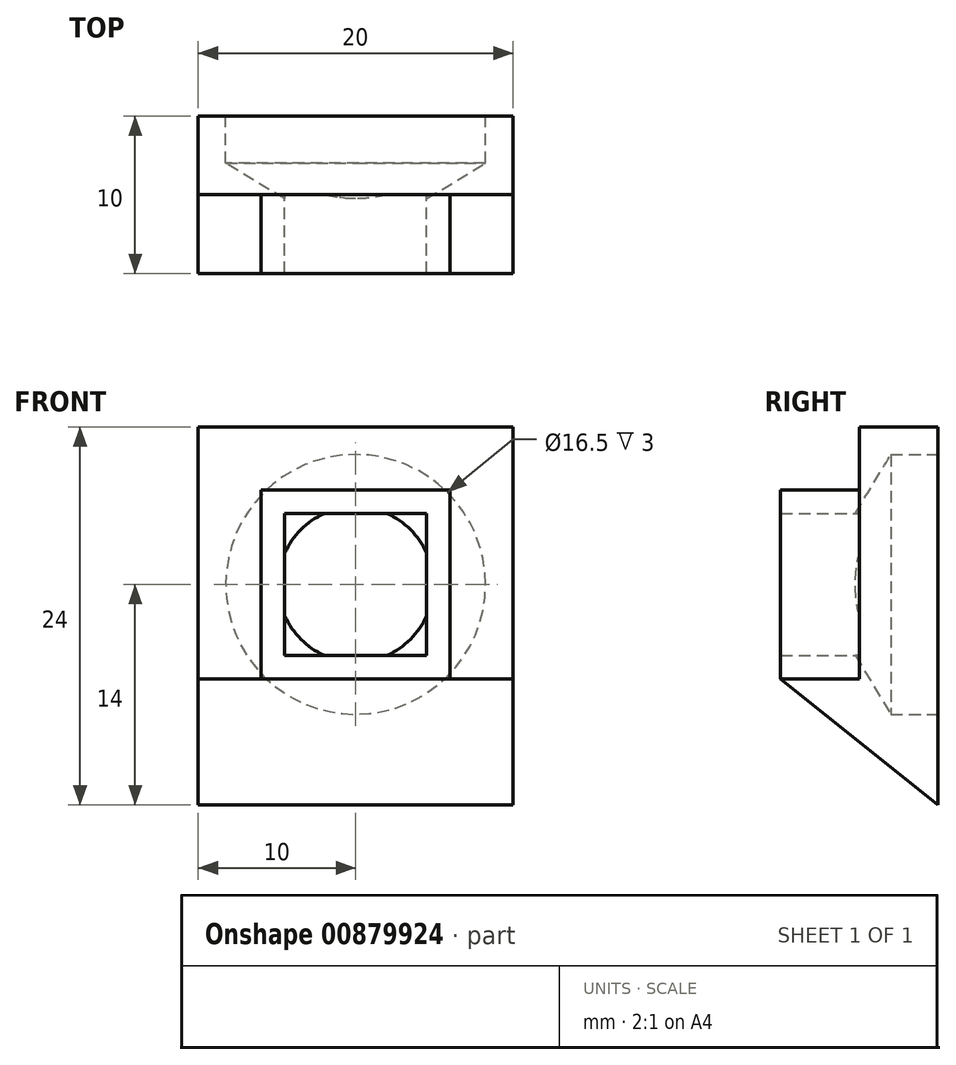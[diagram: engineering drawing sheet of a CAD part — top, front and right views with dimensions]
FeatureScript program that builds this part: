
annotation { "Feature Type Name" : "Feature", "Feature Type Description" : "" }
export const myFeature = defineFeature(function(context is Context, id is Id, definition is map)
    precondition{}
    {
        {
            var Q0;
            Q0=qCreatedBy(makeId("Front.planeOp"),FACE);
            var sketch = newSketch(context, id + "F0", { "sketchPlane" : qUnion([Q0])});
            skLineSegment(sketch, "E0.bottom", {"start": v(10, 10) * mm, "end": v(-10, 10) * mm});
            skLineSegment(sketch, "E0.top", {"start": v(10, -10) * mm, "end": v(-10, -10) * mm});
            skLineSegment(sketch, "E0.left", {"start": v(10, 10) * mm, "end": v(10, -10) * mm});
            skLineSegment(sketch, "E0.right", {"start": v(-10, 10) * mm, "end": v(-10, -10) * mm});
            skPoint(sketch, "E0.middle", {"position": v(0, 0) * mm});
            skSolve(sketch);
        }
        {
            var Q0;
            Q0=makeQuery(id+"F0.imprint","IMPRINT",FACE,{"disambiguationData":[TD([[makeQuery(id+"F0.imprint","IMPRINT",EDGE,{"derivedFrom":sQuery(id+"F0.wireOp",EDGE,"E0.bottom")}),1.0]])]});
            extrude(context, id + "F1", {"entities" : qUnion([Q0]), "depth" : 5 * mm, "offsetDistance" : 25 * mm});
        }
        {
            var Q0;
            Q0=makeQuery(id+"F1.opExtrude","CAP_FACE",FACE,{"disambiguationData":[OSD([sQuery(id+"F0.wireOp",EDGE,"E0.bottom"),sQuery(id+"F0.wireOp",EDGE,"E0.top"),sQuery(id+"F0.wireOp",EDGE,"E0.left"),sQuery(id+"F0.wireOp",EDGE,"E0.right")])],"isStart":false});
            var sketch = newSketch(context, id + "F2", { "sketchPlane" : qUnion([Q0])});
            skLineSegment(sketch, "E1.bottom", {"start": v(-6, 6) * mm, "end": v(6, 6) * mm});
            skLineSegment(sketch, "E1.top", {"start": v(-6, -6) * mm, "end": v(6, -6) * mm});
            skLineSegment(sketch, "E1.left", {"start": v(-6, 6) * mm, "end": v(-6, -6) * mm});
            skLineSegment(sketch, "E1.right", {"start": v(6, 6) * mm, "end": v(6, -6) * mm});
            skPoint(sketch, "E1.middle", {"position": v(0, 0) * mm});
            skLineSegment(sketch, "E2.bottom", {"start": v(-4.5, 4.5) * mm, "end": v(4.5, 4.5) * mm});
            skLineSegment(sketch, "E2.top", {"start": v(-4.5, -4.5) * mm, "end": v(4.5, -4.5) * mm});
            skLineSegment(sketch, "E2.left", {"start": v(-4.5, 4.5) * mm, "end": v(-4.5, -4.5) * mm});
            skLineSegment(sketch, "E2.right", {"start": v(4.5, 4.5) * mm, "end": v(4.5, -4.5) * mm});
            skSolve(sketch);
        }
        {
            var Q0;
            Q0=makeQuery(id+"F2.imprint","IMPRINT",FACE,{"disambiguationData":[TD([[makeQuery(id+"F2.imprint","IMPRINT",EDGE,{"derivedFrom":sQuery(id+"F2.wireOp",EDGE,"E1.bottom")}),-1.0]])]});
            extrude(context, id + "F3", {"entities" : qUnion([Q0]), "operationType" : NewBodyOperationType.ADD, "depth" : 5 * mm, "offsetDistance" : 25 * mm});
        }
        {
            var Q0;
            Q0=makeQuery(id+"F1.opExtrude","CAP_FACE",FACE,{"disambiguationData":[OSD([sQuery(id+"F0.wireOp",EDGE,"E0.bottom"),sQuery(id+"F0.wireOp",EDGE,"E0.top"),sQuery(id+"F0.wireOp",EDGE,"E0.left"),sQuery(id+"F0.wireOp",EDGE,"E0.right")])],"isStart":true});
            var sketch = newSketch(context, id + "F4", { "sketchPlane" : qUnion([Q0])});
            skCircle(sketch, "E3", {"center": v(0, 0) * mm, "radius": 8.25 * mm});
            skSolve(sketch);
        }
        {
            var Q0;
            Q0=sQuery(id+"F4.wireOp",VERTEX,"E3.center");
            var Q1;
            Q1=makeQuery(id+"F1.opExtrude","SWEPT_BODY",BODY,{"disambiguationData":[OSD([sQuery(id+"F0.wireOp",EDGE,"E0.bottom"),sQuery(id+"F0.wireOp",EDGE,"E0.top"),sQuery(id+"F0.wireOp",EDGE,"E0.left"),sQuery(id+"F0.wireOp",EDGE,"E0.right")])]});
            hole(context, id + "F5", {"style" : HoleStyle.SIMPLE, "endStyle" : HoleEndStyle.BLIND, "holeDiameter" : 16.5 * mm, "majorDiameter" : 5 * mm, "holeDepth" : 3 * mm, "isTappedThrough" : true, "tappedDepth" : 12 * mm, "tapClearance" : 3, "locations" : qUnion([Q0]), "scope" : qUnion([Q1])});
        }
        {
            var Q0;
            {var subQ0=sQuery(id+"F0.wireOp",EDGE,"E0.left");var subQ1=sQuery(id+"F0.wireOp",EDGE,"E0.top");var subQ2=sQuery(id+"F0.wireOp",EDGE,"E0.right");var subQ3=sQuery(id+"F0.wireOp",EDGE,"E0.bottom");Q0=makeQuery(id+"F3.boolean.opBoolean","SPLIT",FACE,{"disambiguationData":[TD([makeQuery(id+"F1.opExtrude","SWEPT_FACE",FACE,{"disambiguationData":[OSD([subQ3])]})])],"derivedFrom":makeQuery(id+"F1.opExtrude","CAP_FACE",FACE,{"disambiguationData":[OSD([subQ3,subQ1,subQ0,subQ2])],"isStart":false})});}
            var sketch = newSketch(context, id + "F6", { "sketchPlane" : qUnion([Q0])});
            skPoint(sketch, "E4.oppositeSnap0", {"position": v(0, -6) * mm});
            skLineSegment(sketch, "E4.bottom", {"start": v(-10, -10) * mm, "end": v(10, -10) * mm});
            skLineSegment(sketch, "E4.top", {"start": v(-10, -6) * mm, "end": v(10, -6) * mm});
            skLineSegment(sketch, "E4.left", {"start": v(-10, -10) * mm, "end": v(-10, -6) * mm});
            skLineSegment(sketch, "E4.right", {"start": v(10, -10) * mm, "end": v(10, -6) * mm});
            skSolve(sketch);
        }
        {
            var Q0;
            Q0 = qSketchRegion(id + "F6", true);
            extrude(context, id + "F7", {"entities" : qUnion([Q0]), "operationType" : NewBodyOperationType.ADD, "depth" : 5 * mm, "offsetDistance" : 25 * mm});
        }
        {
            var Q0;
            Q0=makeQuery(id+"F7.boolean.opBoolean","MERGE",FACE,{"derivedFrom":[makeQuery(id+"F1.opExtrude","SWEPT_FACE",FACE,{"disambiguationData":[OSD([sQuery(id+"F0.wireOp",EDGE,"E0.right")])]}),makeQuery(id+"F7.opExtrude","SWEPT_FACE",FACE,{"disambiguationData":[OSD([sQuery(id+"F6.wireOp",EDGE,"E4.left")])]})]});
            var sketch = newSketch(context, id + "F8", { "sketchPlane" : qUnion([Q0])});
            skLineSegment(sketch, "E5", {"start": v(5, -10) * mm, "end": v(10, -6) * mm});
            skSolve(sketch);
        }
        {
            var Q0;
            {var subQ0=sQuery(id+"F8.wireOp",EDGE,"E5");Q0=makeQuery(id+"F8.imprint","IMPRINT",FACE,{"disambiguationData":[TD([[makeQuery(id+"F8.imprint","IMPRINT",EDGE,{"derivedFrom":subQ0}),-1.0]])]});}
            extrude(context, id + "F9", {"entities" : qUnion([Q0]), "operationType" : NewBodyOperationType.REMOVE, "endBound" : BoundingType.THROUGH_ALL, "oppositeDirection" : true, "depth" : 25 * mm, "offsetDistance" : 25 * mm});
        }
        {
            var Q0;
            Q0=makeQuery(id+"F7.boolean.opBoolean","MERGE",FACE,{"derivedFrom":[makeQuery(id+"F1.opExtrude","SWEPT_FACE",FACE,{"disambiguationData":[OSD([sQuery(id+"F0.wireOp",EDGE,"E0.right")])]}),makeQuery(id+"F7.opExtrude","SWEPT_FACE",FACE,{"disambiguationData":[OSD([sQuery(id+"F6.wireOp",EDGE,"E4.left")])]})]});
            var sketch = newSketch(context, id + "F10", { "sketchPlane" : qUnion([Q0])});
            skLineSegment(sketch, "E6", {"start": v(5, -10) * mm, "end": v(0, -14) * mm});
            skLineSegment(sketch, "E7", {"start": v(0, -14) * mm, "end": v(0, -10) * mm});
            skSolve(sketch);
        }
        {
            var Q0;
            Q0 = qSketchRegion(id + "F10", true);
            var Q1;
            Q1=makeQuery(id+"F10.imprint","IMPRINT",FACE,{"disambiguationData":[TD([[makeQuery(id+"F10.imprint","IMPRINT",EDGE,{"derivedFrom":sQuery(id+"F10.wireOp",EDGE,"E6")}),-1.0]])]});
            extrude(context, id + "F11", {"entities" : qUnion([Q0, Q1]), "operationType" : NewBodyOperationType.ADD, "oppositeDirection" : true, "depth" : 20 * mm, "offsetDistance" : 25 * mm});
        }
    });
